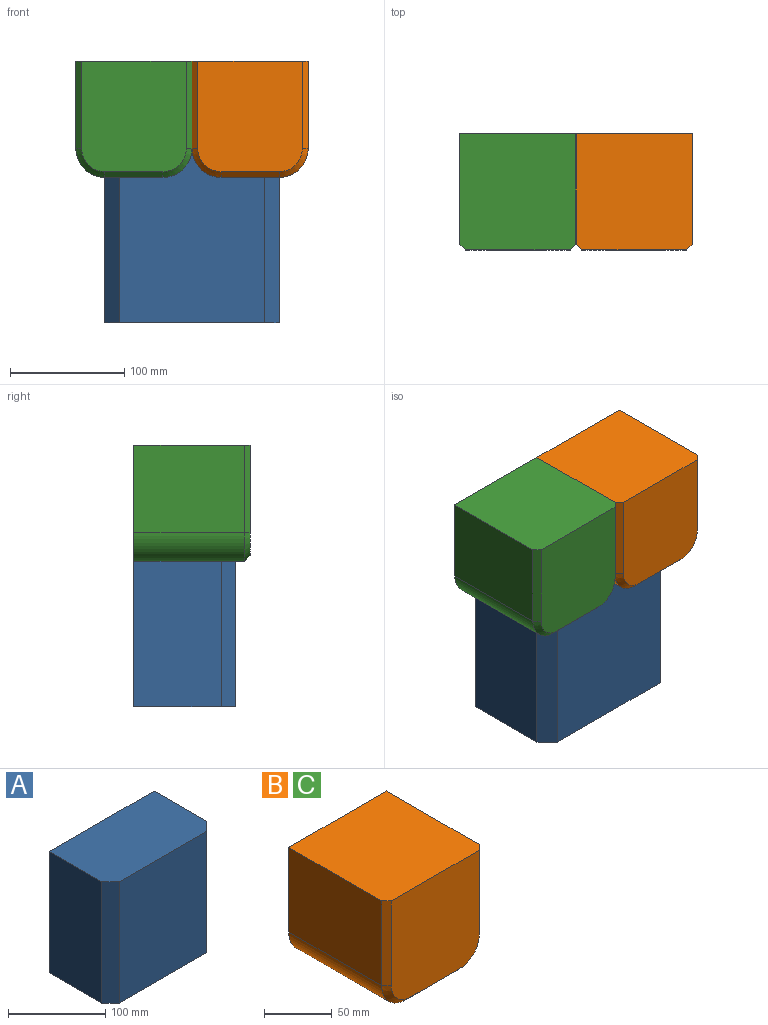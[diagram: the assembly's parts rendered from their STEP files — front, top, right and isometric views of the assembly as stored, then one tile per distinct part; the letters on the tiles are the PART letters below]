
ASSEMBLY  parts=3 mates=2
PART A: 8 faces, bbox 152.4x88.9x152.4 mm
  f0: plane 152.4x88.9mm, normal (0,0,1), area 13387.1mm2, adj f1,f3,f4,f5,f6,f7
  f1: plane 152.4x76.2mm, normal (-1,0,0), area 11612.9mm2, adj f0,f2,f5,f6
  f2: plane 152.4x88.9mm, normal (0,0,-1), area 13387.1mm2, adj f1,f3,f4,f5,f6,f7
  f3: plane 152.4x76.2mm, normal (1,0,0), area 11612.9mm2, adj f0,f2,f5,f7
  f4: plane 152.4x127mm, normal (0,-1,0), area 19354.8mm2, adj f0,f2,f6,f7
  f5: plane 152.4x152.4mm, normal (0,1,0), area 23225.8mm2, adj f0,f1,f2,f3
  f6: plane 152.4x12.7mm, normal (-0.71,-0.71,0), area 2737.2mm2, adj f0,f1,f2,f4
  f7: plane 152.4x12.7mm, normal (0.71,-0.71,0), area 2737.2mm2, adj f0,f2,f3,f4
PART B: 13 faces, bbox 101.6x101.6x101.6 mm
  f0: plane 101.6x101.6mm, normal (0,0,1), area 10296.8mm2, adj f1,f3,f4,f5,f6,f8
  f1: plane 96.52x76.2mm, normal (-1,0,0), area 7354.8mm2, adj f0,f5,f6,f9
  f2: plane 96.52x50.8mm, normal (0,0,-1), area 4903.2mm2, adj f5,f7,f9,f10
  f3: plane 96.52x76.2mm, normal (1,0,0), area 7354.8mm2, adj f0,f5,f8,f10
  f4: plane 96.52x91.44mm, normal (0,-1,0), area 8648.6mm2, adj f0,f6,f7,f8,f11,f12
  f5: plane 101.6x101.6mm, normal (0,1,0), area 10045.7mm2, adj f0,f1,f2,f3,f9,f10
  f6: plane 76.2x5.08mm, normal (-0.71,-0.71,0), area 547.4mm2, adj f0,f1,f4,f12
  f7: plane 50.8x5.08mm, normal (0,-0.71,-0.71), area 365mm2, adj f2,f4,f11,f12
  f8: plane 76.2x5.08mm, normal (0.71,-0.71,0), area 547.4mm2, adj f0,f3,f4,f11
  f9: cylinder r=25.4mm len=96.52mm, axis (0,1,0), area 3851mm2, adj f1,f2,f5,f12
  f10: cylinder r=25.4mm len=96.52mm, axis (0,-1,0), area 3851mm2, adj f2,f3,f5,f11
  f11: cone r=20.32mm half-angle=45deg, axis (0,1,0), area 258mm2, adj f4,f7,f8,f10
  f12: cone r=20.32mm half-angle=45deg, axis (0,1,0), area 258mm2, adj f4,f6,f7,f9
PART C: same geometry as B
PLACE A t=(83.81,-7.56,-111.02)mm
PLACE B t=(134.61,-13.91,-9.42)mm
PLACE C t=(33.01,-13.91,-9.42)mm
MATE fastened C.f5 <-> A.f5  axis (0,1,0) through (83.81,36.89,-34.82)mm
MATE fastened C.f3 <-> B.f1  axis (1,0,0) through (83.81,-11.37,3.28)mm
